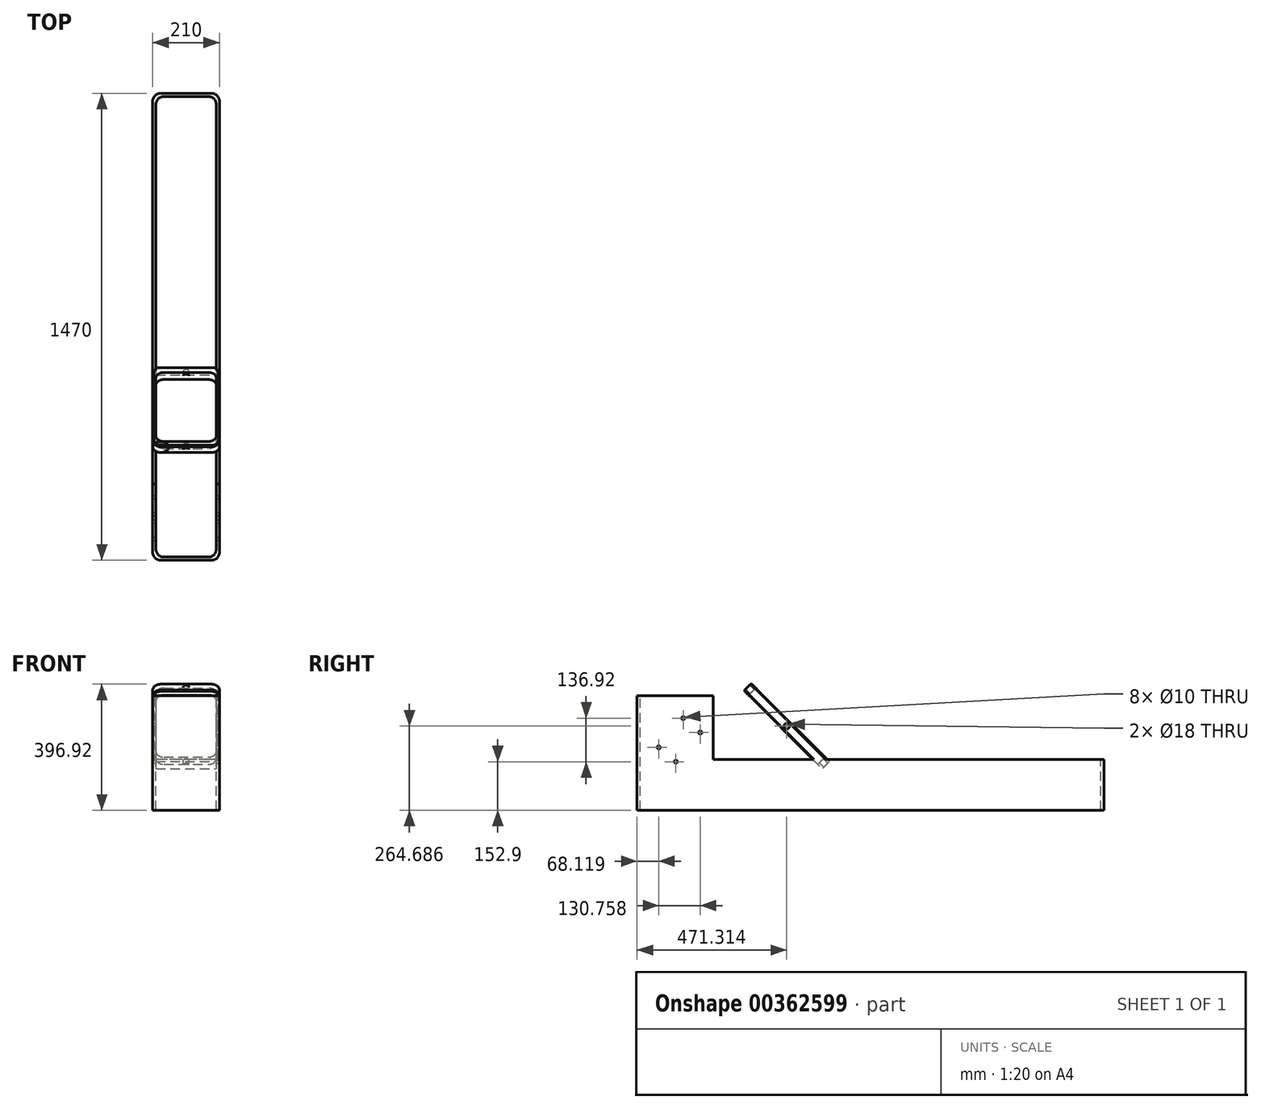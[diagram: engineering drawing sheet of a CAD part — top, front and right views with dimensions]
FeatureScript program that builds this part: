
annotation { "Feature Type Name" : "Feature", "Feature Type Description" : "" }
export const myFeature = defineFeature(function(context is Context, id is Id, definition is map)
    precondition{}
    {
        {
            var Q0;
            Q0=qCreatedBy(makeId("Front.planeOp"),FACE);
            var sketch = newSketch(context, id + "F0", { "sketchPlane" : qUnion([Q0])});
            skLineSegment(sketch, "E0.bottom", {"start": v(-105, 16) * mm, "end": v(105, 16) * mm});
            skLineSegment(sketch, "E0.top", {"start": v(-105, -174) * mm, "end": v(105, -174) * mm});
            skLineSegment(sketch, "E0.left", {"start": v(-105, 16) * mm, "end": v(-105, -174) * mm});
            skLineSegment(sketch, "E0.right", {"start": v(105, 16) * mm, "end": v(105, -174) * mm});
            skPoint(sketch, "E1", {"position": v(0, 16) * mm});
            skLineSegment(sketch, "E2.bottom", {"start": v(-95, 16) * mm, "end": v(95, 16) * mm});
            skLineSegment(sketch, "E2.top", {"start": v(-95, -154) * mm, "end": v(95, -154) * mm});
            skLineSegment(sketch, "E2.left", {"start": v(-95, 16) * mm, "end": v(-95, -154) * mm});
            skLineSegment(sketch, "E2.right", {"start": v(95, 16) * mm, "end": v(95, -154) * mm});
            skLineSegment(sketch, "E3.MirrorCS", {"start": v(-95, -16) * mm, "end": v(-95, 154) * mm});
            skLineSegment(sketch, "E4.MirrorCS", {"start": v(-95, 154) * mm, "end": v(95, 154) * mm});
            skLineSegment(sketch, "E5.MirrorCS", {"start": v(95, -16) * mm, "end": v(95, 154) * mm});
            skLineSegment(sketch, "E6.MirrorCS", {"start": v(105, -16) * mm, "end": v(105, 174) * mm});
            skLineSegment(sketch, "E7.MirrorCS", {"start": v(-105, 174) * mm, "end": v(105, 174) * mm});
            skLineSegment(sketch, "E8.MirrorCS", {"start": v(-105, -16) * mm, "end": v(-105, 174) * mm});
            skSolve(sketch);
        }
        {
            var Q0;
            Q0=makeQuery(id+"F0.imprint","IMPRINT",FACE,{"disambiguationData":[TD([[makeQuery(id+"F0.imprint","IMPRINT",EDGE,{"derivedFrom":sQuery(id+"F0.wireOp",EDGE,"E0.top")}),1.0]])]});
            var Q1;
            {var subQ0=sQuery(id+"F0.wireOp",EDGE,"E4.MirrorCS");Q1=makeQuery(id+"F0.imprint","IMPRINT",FACE,{"disambiguationData":[TD([[makeQuery(id+"F0.imprint","IMPRINT",EDGE,{"derivedFrom":subQ0}),1.0]])]});}
            extrude(context, id + "F1", {"entities" : qUnion([Q0, Q1]), "endBound" : BoundingType.SYMMETRIC, "depth" : 32 * mm});
        }
        {
            var Q0;
            Q0=makeQuery(id+"F1.opExtrude","SWEPT_FACE",FACE,{"disambiguationData":[OSD([sQuery(id+"F0.wireOp",EDGE,"E0.right")])]});
            var sketch = newSketch(context, id + "F2", { "sketchPlane" : qUnion([Q0])});
            skPoint(sketch, "E9", {"position": v(0, 0) * mm});
            skSolve(sketch);
        }
        {
            var Q0;
            Q0=sQuery(id+"F2.wireOp",VERTEX,"E9");
            var Q1;
            Q1=makeQuery(id+"F1.opExtrude","SWEPT_BODY",BODY,{"disambiguationData":[OSD([sQuery(id+"F0.wireOp",EDGE,"E0.bottom"),sQuery(id+"F0.wireOp",EDGE,"E0.top"),sQuery(id+"F0.wireOp",EDGE,"E0.left"),sQuery(id+"F0.wireOp",EDGE,"E0.right"),sQuery(id+"F0.wireOp",EDGE,"E2.top"),sQuery(id+"F0.wireOp",EDGE,"E2.left"),sQuery(id+"F0.wireOp",EDGE,"E2.right")])]});
            hole(context, id + "F3", {"style" : HoleStyle.SIMPLE, "endStyle" : HoleEndStyle.THROUGH, "holeDiameter" : 18 * mm, "isTappedThrough" : true, "tappedDepth" : 12 * mm, "tapClearance" : 3, "locations" : qUnion([Q0]), "scope" : qUnion([Q1])});
        }
        {
            var Q0;
            Q0=makeQuery(id+"F1.opExtrude","SWEPT_FACE",FACE,{"disambiguationData":[OSD([sQuery(id+"F0.wireOp",EDGE,"E7.MirrorCS")])]});
            var sketch = newSketch(context, id + "F4", { "sketchPlane" : qUnion([Q0])});
            skCircle(sketch, "E10", {"center": v(0, 0) * mm, "radius": 9 * mm});
            skSolve(sketch);
        }
        {
            var Q0;
            Q0=sQuery(id+"F4.wireOp",VERTEX,"E10.center");
            var Q1;
            Q1=makeQuery(id+"F1.opExtrude","SWEPT_BODY",BODY,{"disambiguationData":[OSD([sQuery(id+"F0.wireOp",EDGE,"E0.top"),sQuery(id+"F0.wireOp",EDGE,"E0.left"),sQuery(id+"F0.wireOp",EDGE,"E0.right"),sQuery(id+"F0.wireOp",EDGE,"E2.top"),sQuery(id+"F0.wireOp",EDGE,"E2.left"),sQuery(id+"F0.wireOp",EDGE,"E2.right"),sQuery(id+"F0.wireOp",EDGE,"E3.MirrorCS"),sQuery(id+"F0.wireOp",EDGE,"E4.MirrorCS"),sQuery(id+"F0.wireOp",EDGE,"E5.MirrorCS"),sQuery(id+"F0.wireOp",EDGE,"E6.MirrorCS"),sQuery(id+"F0.wireOp",EDGE,"E7.MirrorCS"),sQuery(id+"F0.wireOp",EDGE,"E8.MirrorCS")])]});
            hole(context, id + "F5", {"style" : HoleStyle.SIMPLE, "endStyle" : HoleEndStyle.THROUGH, "holeDiameter" : 18 * mm, "isTappedThrough" : true, "tappedDepth" : 12 * mm, "tapClearance" : 3, "locations" : qUnion([Q0]), "scope" : qUnion([Q1])});
        }
        {
            var Q0;
            Q0=makeQuery(id+"F1.opExtrude","SWEPT_BODY",BODY,{"disambiguationData":[OSD([sQuery(id+"F0.wireOp",EDGE,"E0.top"),sQuery(id+"F0.wireOp",EDGE,"E0.left"),sQuery(id+"F0.wireOp",EDGE,"E0.right"),sQuery(id+"F0.wireOp",EDGE,"E2.top"),sQuery(id+"F0.wireOp",EDGE,"E2.left"),sQuery(id+"F0.wireOp",EDGE,"E2.right"),sQuery(id+"F0.wireOp",EDGE,"E3.MirrorCS"),sQuery(id+"F0.wireOp",EDGE,"E4.MirrorCS"),sQuery(id+"F0.wireOp",EDGE,"E5.MirrorCS"),sQuery(id+"F0.wireOp",EDGE,"E6.MirrorCS"),sQuery(id+"F0.wireOp",EDGE,"E7.MirrorCS"),sQuery(id+"F0.wireOp",EDGE,"E8.MirrorCS")])]});
            var Q1;
            Q1=sQuery(id+"F0.wireOp",EDGE,"E2.bottom");
            transform(context, id + "F6", {"entities" : qUnion([Q0]), "transformType" : TransformType.ROTATION, "transformAxis" : qUnion([Q1]), "angle" : 45 * degree, "makeCopy" : false});
        }
        {
            var Q0;
            Q0=qCreatedBy(makeId("Top.planeOp"),FACE);
            var sketch = newSketch(context, id + "F7", { "sketchPlane" : qUnion([Q0])});
            skLineSegment(sketch, "E11", {"start": v(0, 952.41) * mm, "end": v(0, -490.38) * mm, "construction": true});
            skLineSegment(sketch, "E12.right", {"start": v(-105, 1010) * mm, "end": v(-105, -460) * mm});
            skPoint(sketch, "E12.middle", {"position": v(0, 0) * mm});
            skLineSegment(sketch, "E13", {"start": v(-105, 1010) * mm, "end": v(0, 1010) * mm});
            skLineSegment(sketch, "E14", {"start": v(-105, -460) * mm, "end": v(0, -460) * mm});
            skLineSegment(sketch, "E15", {"start": v(0, 1000) * mm, "end": v(-95, 1000) * mm});
            skLineSegment(sketch, "E16", {"start": v(-95, 1000) * mm, "end": v(-95, -450) * mm});
            skLineSegment(sketch, "E17", {"start": v(-95, -450) * mm, "end": v(0, -450) * mm});
            skLineSegment(sketch, "E18.MirrorCS", {"start": v(0, 1000) * mm, "end": v(95, 1000) * mm});
            skLineSegment(sketch, "E19.MirrorCS", {"start": v(105, 1010) * mm, "end": v(0, 1010) * mm});
            skLineSegment(sketch, "E20.MirrorCS", {"start": v(105, -460) * mm, "end": v(0, -460) * mm});
            skLineSegment(sketch, "E21.MirrorCS", {"start": v(95, -450) * mm, "end": v(0, -450) * mm});
            skLineSegment(sketch, "E22.MirrorCS", {"start": v(95, 1000) * mm, "end": v(95, -450) * mm});
            skLineSegment(sketch, "E23.MirrorCS", {"start": v(105, 1010) * mm, "end": v(105, -460) * mm});
            skLineSegment(sketch, "E24", {"start": v(-165.34, 0) * mm, "end": v(160.71, 0) * mm, "construction": true});
            skLineSegment(sketch, "E25", {"start": v(-209.51, -220) * mm, "end": v(228, -220) * mm, "construction": true});
            skLineSegment(sketch, "E26", {"start": v(-105, -220) * mm, "end": v(-95, -220) * mm});
            skLineSegment(sketch, "E27", {"start": v(95, -220) * mm, "end": v(105, -220) * mm});
            skSolve(sketch);
        }
        {
            var Q0;
            Q0=makeQuery(id+"F7.imprint","IMPRINT",FACE,{"disambiguationData":[TD([[makeQuery(id+"F7.imprint","IMPRINT",EDGE,{"derivedFrom":sQuery(id+"F7.wireOp",EDGE,"E12.right")}),1.0]])]});
            extrude(context, id + "F8", {"entities" : qUnion([Q0]), "operationType" : NewBodyOperationType.ADD, "oppositeDirection" : true, "depth" : 260 * mm, "hasSecondDirection" : true, "secondDirectionOppositeDirection" : true, "secondDirectionDepth" : 100 * mm});
        }
        {
            var Q0;
            {var subQ1=sQuery(id+"F7.wireOp",EDGE,"E14");Q0=makeQuery(id+"F7.imprint","IMPRINT",FACE,{"disambiguationData":[TD([[makeQuery(id+"F7.imprint","IMPRINT",EDGE,{"derivedFrom":subQ1}),1.0]])]});}
            extrude(context, id + "F9", {"entities" : qUnion([Q0]), "operationType" : NewBodyOperationType.ADD, "depth" : 100 * mm, "hasSecondDirection" : true, "secondDirectionOppositeDirection" : true, "secondDirectionDepth" : 100 * mm});
        }
        {
            var Q0;
            Q0=makeQuery(id+"F1.opExtrude","SWEPT_EDGE",EDGE,{"disambiguationData":[OSD([sQuery(id+"F0.wireOp",EDGE,"E2.top"),sQuery(id+"F0.wireOp",EDGE,"E2.left")])]});
            var Q1;
            Q1=makeQuery(id+"F1.opExtrude","SWEPT_EDGE",EDGE,{"disambiguationData":[OSD([sQuery(id+"F0.wireOp",EDGE,"E2.top"),sQuery(id+"F0.wireOp",EDGE,"E2.right")])]});
            var Q2;
            Q2=makeQuery(id+"F1.opExtrude","SWEPT_EDGE",EDGE,{"disambiguationData":[OSD([sQuery(id+"F0.wireOp",EDGE,"E4.MirrorCS"),sQuery(id+"F0.wireOp",EDGE,"E5.MirrorCS")])]});
            var Q3;
            Q3=makeQuery(id+"F1.opExtrude","SWEPT_EDGE",EDGE,{"disambiguationData":[OSD([sQuery(id+"F0.wireOp",EDGE,"E6.MirrorCS"),sQuery(id+"F0.wireOp",EDGE,"E7.MirrorCS")])]});
            var Q4;
            Q4=makeQuery(id+"F1.opExtrude","SWEPT_EDGE",EDGE,{"disambiguationData":[OSD([sQuery(id+"F0.wireOp",EDGE,"E3.MirrorCS"),sQuery(id+"F0.wireOp",EDGE,"E4.MirrorCS")])]});
            var Q5;
            Q5=makeQuery(id+"F1.opExtrude","SWEPT_EDGE",EDGE,{"disambiguationData":[OSD([sQuery(id+"F0.wireOp",EDGE,"E7.MirrorCS"),sQuery(id+"F0.wireOp",EDGE,"E8.MirrorCS")])]});
            var Q6;
            Q6=makeQuery(id+"F8.opExtrude","SWEPT_EDGE",EDGE,{"disambiguationData":[OSD([sQuery(id+"F7.wireOp",EDGE,"E16"),sQuery(id+"F7.wireOp",EDGE,"E17")])]});
            var Q7;
            Q7=makeQuery(id+"F8.opExtrude","SWEPT_EDGE",EDGE,{"disambiguationData":[OSD([sQuery(id+"F7.wireOp",EDGE,"E21.MirrorCS"),sQuery(id+"F7.wireOp",EDGE,"E22.MirrorCS")])]});
            var Q8;
            Q8=makeQuery(id+"F8.opExtrude","SWEPT_EDGE",EDGE,{"disambiguationData":[OSD([sQuery(id+"F7.wireOp",EDGE,"E18.MirrorCS"),sQuery(id+"F7.wireOp",EDGE,"E22.MirrorCS")])]});
            var Q9;
            Q9=makeQuery(id+"F8.opExtrude","SWEPT_EDGE",EDGE,{"disambiguationData":[OSD([sQuery(id+"F7.wireOp",EDGE,"E15"),sQuery(id+"F7.wireOp",EDGE,"E16")])]});
            var Q10;
            Q10=makeQuery(id+"F8.opExtrude","SWEPT_EDGE",EDGE,{"disambiguationData":[OSD([sQuery(id+"F7.wireOp",EDGE,"E12.right"),sQuery(id+"F7.wireOp",EDGE,"E14")])]});
            var Q11;
            Q11=makeQuery(id+"F8.opExtrude","SWEPT_EDGE",EDGE,{"disambiguationData":[OSD([sQuery(id+"F7.wireOp",EDGE,"E20.MirrorCS"),sQuery(id+"F7.wireOp",EDGE,"E23.MirrorCS")])]});
            var Q12;
            Q12=makeQuery(id+"F8.opExtrude","SWEPT_EDGE",EDGE,{"disambiguationData":[OSD([sQuery(id+"F7.wireOp",EDGE,"E19.MirrorCS"),sQuery(id+"F7.wireOp",EDGE,"E23.MirrorCS")])]});
            var Q13;
            Q13=makeQuery(id+"F8.opExtrude","SWEPT_EDGE",EDGE,{"disambiguationData":[OSD([sQuery(id+"F7.wireOp",EDGE,"E12.right"),sQuery(id+"F7.wireOp",EDGE,"E13")])]});
            fillet(context, id + "F10", {"entities" : qUnion([Q0, Q1, Q2, Q3, Q4, Q5, Q6, Q7, Q8, Q9, Q10, Q11, Q12, Q13]), "radius" : 25 * mm, "tangentPropagation" : true, "allowEdgeOverflow" : false});
        }
        {
            var Q0;
            {var subQ0=sQuery(id+"F0.wireOp",EDGE,"E7.MirrorCS");var subQ1=sQuery(id+"F0.wireOp",EDGE,"E6.MirrorCS");Q0=makeQuery(id+"F10.opFillet","BLEND_EDGE",EDGE,{"blendedFrom":[makeQuery(id+"F1.opExtrude","SWEPT_EDGE",EDGE,{"disambiguationData":[OSD([subQ1,subQ0])]}),makeQuery(id+"F1.opExtrude","CAP_FACE",FACE,{"disambiguationData":[OSD([sQuery(id+"F0.wireOp",EDGE,"E0.top"),sQuery(id+"F0.wireOp",EDGE,"E0.left"),sQuery(id+"F0.wireOp",EDGE,"E0.right"),sQuery(id+"F0.wireOp",EDGE,"E2.top"),sQuery(id+"F0.wireOp",EDGE,"E2.left"),sQuery(id+"F0.wireOp",EDGE,"E2.right"),sQuery(id+"F0.wireOp",EDGE,"E3.MirrorCS"),sQuery(id+"F0.wireOp",EDGE,"E4.MirrorCS"),sQuery(id+"F0.wireOp",EDGE,"E5.MirrorCS"),subQ1,subQ0,sQuery(id+"F0.wireOp",EDGE,"E8.MirrorCS")])],"isStart":true})],"blendedInto":[makeQuery(id+"F1.opExtrude","CAP_FACE",FACE,{"disambiguationData":[OSD([sQuery(id+"F0.wireOp",EDGE,"E0.top"),sQuery(id+"F0.wireOp",EDGE,"E0.left"),sQuery(id+"F0.wireOp",EDGE,"E0.right"),sQuery(id+"F0.wireOp",EDGE,"E2.top"),sQuery(id+"F0.wireOp",EDGE,"E2.left"),sQuery(id+"F0.wireOp",EDGE,"E2.right"),sQuery(id+"F0.wireOp",EDGE,"E3.MirrorCS"),sQuery(id+"F0.wireOp",EDGE,"E4.MirrorCS"),sQuery(id+"F0.wireOp",EDGE,"E5.MirrorCS"),subQ1,subQ0,sQuery(id+"F0.wireOp",EDGE,"E8.MirrorCS")])],"isStart":true})]});}
            var Q1;
            {var subQ1=sQuery(id+"F0.wireOp",EDGE,"E5.MirrorCS");var subQ2=sQuery(id+"F0.wireOp",EDGE,"E2.right");var subQ3=sQuery(id+"F0.wireOp",EDGE,"E7.MirrorCS");var subQ5=sQuery(id+"F0.wireOp",EDGE,"E4.MirrorCS");var subQ6=sQuery(id+"F0.wireOp",EDGE,"E8.MirrorCS");var subQ7=sQuery(id+"F0.wireOp",EDGE,"E0.left");var subQ8=sQuery(id+"F0.wireOp",EDGE,"E6.MirrorCS");var subQ9=sQuery(id+"F0.wireOp",EDGE,"E0.right");var subQ11=sQuery(id+"F0.wireOp",EDGE,"E3.MirrorCS");var subQ12=sQuery(id+"F0.wireOp",EDGE,"E2.left");Q1=makeQuery(id+"F10.opFillet","BLEND_EDGE",EDGE,{"blendedFrom":[makeQuery(id+"F1.opExtrude","SWEPT_EDGE",EDGE,{"disambiguationData":[OSD([subQ8,subQ3])]}),makeQuery(id+"F8.boolean.opBoolean","SPLIT",FACE,{"disambiguationData":[TD([makeQuery(id+"F1.opExtrude","SWEPT_FACE",FACE,{"disambiguationData":[OSD([subQ5])]})])],"derivedFrom":makeQuery(id+"F1.opExtrude","CAP_FACE",FACE,{"disambiguationData":[OSD([sQuery(id+"F0.wireOp",EDGE,"E0.top"),subQ7,subQ9,sQuery(id+"F0.wireOp",EDGE,"E2.top"),subQ12,subQ2,subQ11,subQ5,subQ1,subQ8,subQ3,subQ6])],"isStart":false})})],"blendedInto":[makeQuery(id+"F8.boolean.opBoolean","SPLIT",FACE,{"disambiguationData":[TD([makeQuery(id+"F1.opExtrude","SWEPT_FACE",FACE,{"disambiguationData":[OSD([subQ5])]})])],"derivedFrom":makeQuery(id+"F1.opExtrude","CAP_FACE",FACE,{"disambiguationData":[OSD([sQuery(id+"F0.wireOp",EDGE,"E0.top"),subQ7,subQ9,sQuery(id+"F0.wireOp",EDGE,"E2.top"),subQ12,subQ2,subQ11,subQ5,subQ1,subQ8,subQ3,subQ6])],"isStart":false})})]});}
            chamfer(context, id + "F11", {"entities" : qUnion([Q0, Q1]), "width" : 3 * mm, "tangentPropagation" : true});
        }
        {
            var Q0;
            Q0=makeQuery(id+"F8.boolean.opBoolean","MERGE",FACE,{"derivedFrom":[makeQuery(id+"F1.opExtrude","SWEPT_FACE",FACE,{"disambiguationData":[OSD([sQuery(id+"F0.wireOp",EDGE,"E0.right"),sQuery(id+"F0.wireOp",EDGE,"E6.MirrorCS")])]}),makeQuery(id+"F8.opExtrude","SWEPT_FACE",FACE,{"disambiguationData":[OSD([sQuery(id+"F7.wireOp",EDGE,"E23.MirrorCS")])]})]});
            var sketch = newSketch(context, id + "F12", { "sketchPlane" : qUnion([Q0])});
            skLineSegment(sketch, "E28.bottom", {"start": v(-338.26, -107.1) * mm, "end": v(-261.12, -15.17) * mm});
            skLineSegment(sketch, "E28.top", {"start": v(-391.88, -62.1) * mm, "end": v(-314.75, 29.82) * mm});
            skLineSegment(sketch, "E28.left", {"start": v(-338.26, -107.1) * mm, "end": v(-391.88, -62.1) * mm});
            skLineSegment(sketch, "E28.right", {"start": v(-261.12, -15.17) * mm, "end": v(-314.75, 29.82) * mm});
            skSolve(sketch);
        }
        {
            var Q0;
            Q0=sQuery(id+"F12.wireOp",VERTEX,"E28.top.end");
            var Q1;
            Q1=sQuery(id+"F12.wireOp",VERTEX,"E28.right.start");
            var Q2;
            Q2=sQuery(id+"F12.wireOp",VERTEX,"E28.bottom.start");
            var Q3;
            Q3=sQuery(id+"F12.wireOp",VERTEX,"E28.left.end");
            var Q4;
            Q4=makeQuery(id+"F1.opExtrude","SWEPT_BODY",BODY,{"disambiguationData":[OSD([sQuery(id+"F0.wireOp",EDGE,"E0.top"),sQuery(id+"F0.wireOp",EDGE,"E0.left"),sQuery(id+"F0.wireOp",EDGE,"E0.right"),sQuery(id+"F0.wireOp",EDGE,"E2.top"),sQuery(id+"F0.wireOp",EDGE,"E2.left"),sQuery(id+"F0.wireOp",EDGE,"E2.right"),sQuery(id+"F0.wireOp",EDGE,"E3.MirrorCS"),sQuery(id+"F0.wireOp",EDGE,"E4.MirrorCS"),sQuery(id+"F0.wireOp",EDGE,"E5.MirrorCS"),sQuery(id+"F0.wireOp",EDGE,"E6.MirrorCS"),sQuery(id+"F0.wireOp",EDGE,"E7.MirrorCS"),sQuery(id+"F0.wireOp",EDGE,"E8.MirrorCS")])]});
            hole(context, id + "F13", {"style" : HoleStyle.SIMPLE, "endStyle" : HoleEndStyle.THROUGH, "holeDiameter" : 10 * mm, "isTappedThrough" : true, "tappedDepth" : 12 * mm, "tapClearance" : 3, "locations" : qUnion([Q0, Q1, Q2, Q3]), "scope" : qUnion([Q4])});
        }
    });
